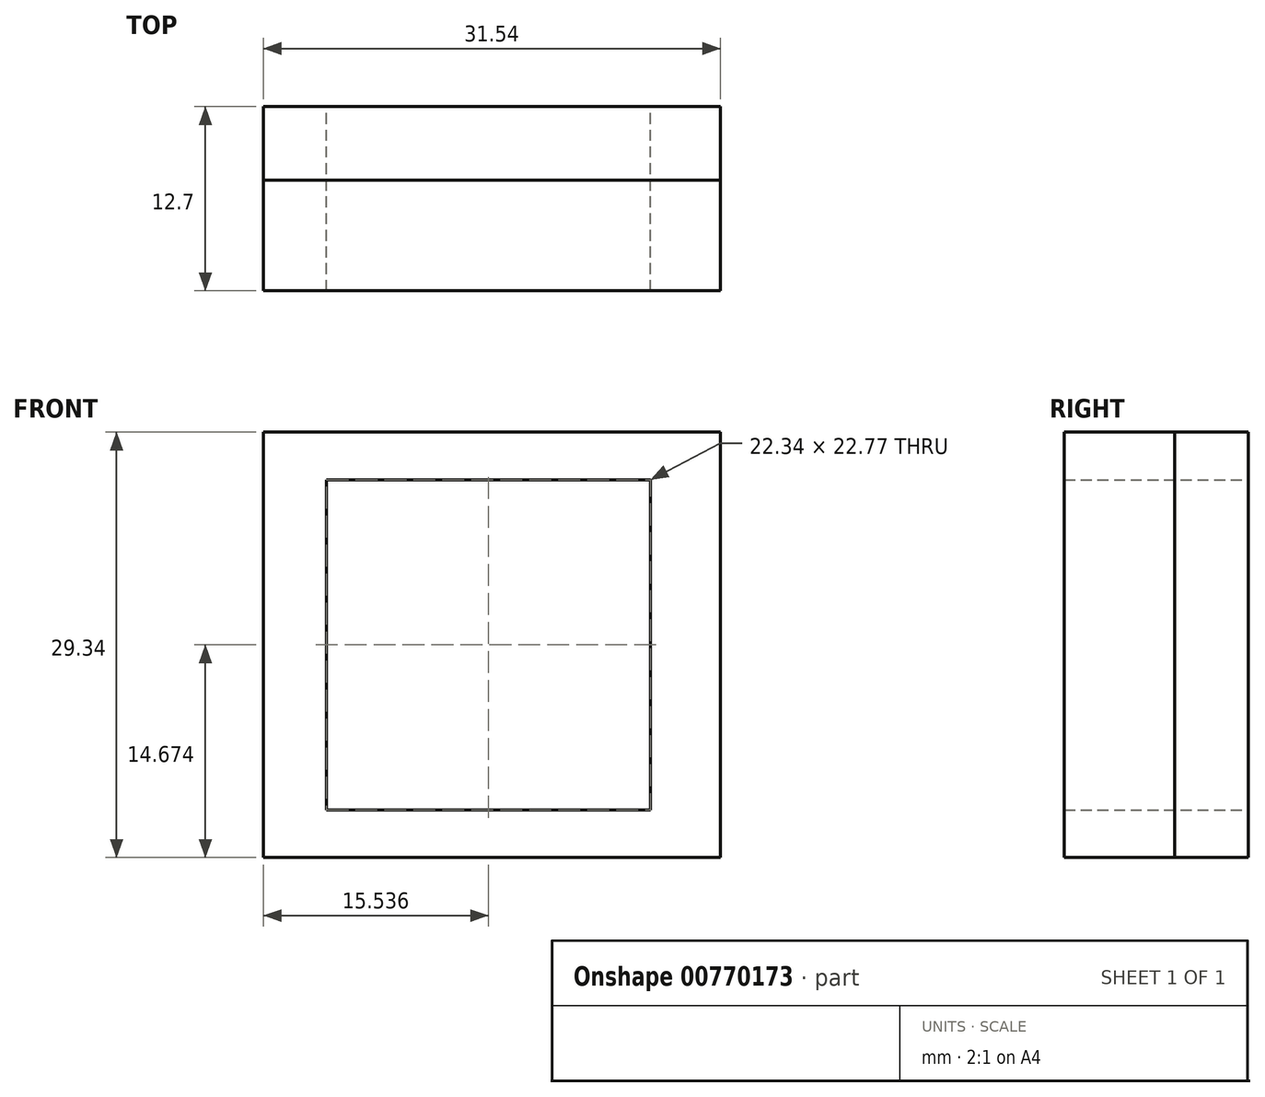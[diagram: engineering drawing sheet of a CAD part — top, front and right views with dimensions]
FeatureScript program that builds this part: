
annotation { "Feature Type Name" : "Feature", "Feature Type Description" : "" }
export const myFeature = defineFeature(function(context is Context, id is Id, definition is map)
    precondition{}
    {
        {
            var Q0;
            Q0=qCreatedBy(makeId("Front.planeOp"),FACE);
            var sketch = newSketch(context, id + "F0", { "sketchPlane" : qUnion([Q0])});
            skLineSegment(sketch, "E0.bottom", {"start": v(-31.7, 21.87) * mm, "end": v(-0.15, 21.87) * mm});
            skLineSegment(sketch, "E0.top", {"start": v(-31.7, -7.47) * mm, "end": v(-0.15, -7.47) * mm});
            skLineSegment(sketch, "E0.left", {"start": v(-31.7, 21.87) * mm, "end": v(-31.7, -7.47) * mm});
            skLineSegment(sketch, "E0.right", {"start": v(-0.15, 21.87) * mm, "end": v(-0.15, -7.47) * mm});
            skLineSegment(sketch, "E1.bottom", {"start": v(-27.32, 18.6) * mm, "end": v(-4.98, 18.6) * mm});
            skLineSegment(sketch, "E1.top", {"start": v(-27.32, -4.18) * mm, "end": v(-4.98, -4.18) * mm});
            skLineSegment(sketch, "E1.left", {"start": v(-27.32, 18.6) * mm, "end": v(-27.32, -4.18) * mm});
            skLineSegment(sketch, "E1.right", {"start": v(-4.98, 18.6) * mm, "end": v(-4.98, -4.18) * mm});
            skSolve(sketch);
        }
        {
            var Q0;
            Q0=makeQuery(id+"F0.imprint","IMPRINT",FACE,{"disambiguationData":[TD([[makeQuery(id+"F0.imprint","IMPRINT",EDGE,{"derivedFrom":sQuery(id+"F0.wireOp",EDGE,"E0.bottom")}),-1.0]])]});
            var Q1;
            Q1 = qSketchRegion(id + "F0", true);
            extrude(context, id + "F1", {"entities" : qUnion([Q0, Q1]), "depth" : 12.7 * mm, "offsetDistance" : 25.4 * mm});
        }
        {
            var Q0;
            Q0 = qSketchRegion(id + "F0", true);
            var Q1;
            Q1=makeQuery(id+"F0.imprint","IMPRINT",FACE,{"disambiguationData":[TD([[makeQuery(id+"F0.imprint","IMPRINT",EDGE,{"derivedFrom":sQuery(id+"F0.wireOp",EDGE,"E1.bottom")}),-1.0]])]});
            extrude(context, id + "F2", {"entities" : qUnion([Q0, Q1]), "depth" : 5.08 * mm, "offsetDistance" : 25.4 * mm});
        }
    });
